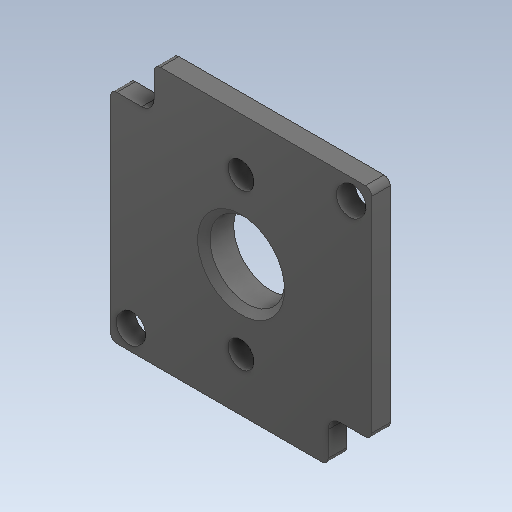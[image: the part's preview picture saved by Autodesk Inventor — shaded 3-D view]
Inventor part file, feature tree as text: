
AUTODESK INVENTOR PART (.ipt)
format: ipt  version: 2020 (Build 240168000, 168)  size: 224,768 bytes
history: native  units: in
note: dims shown in document units (in); Inventor stores cm internally (conversion verified against a paired STEP export)
features: fillet x1
ambient origin geometry x8: Origin, YZ Plane, XZ Plane, XY Plane, X Axis, Y Axis, Z Axis, Center Point
bodies: Solid1 (feature_tree)
feature tree (1):
  fillet  "Fillet4"  [1 undecoded]
note: 1 required parameter value undecoded (feature->parameter linkage not recoverable at this tier; creation-order binding heuristic only, values carry confidence <= 0.55)
